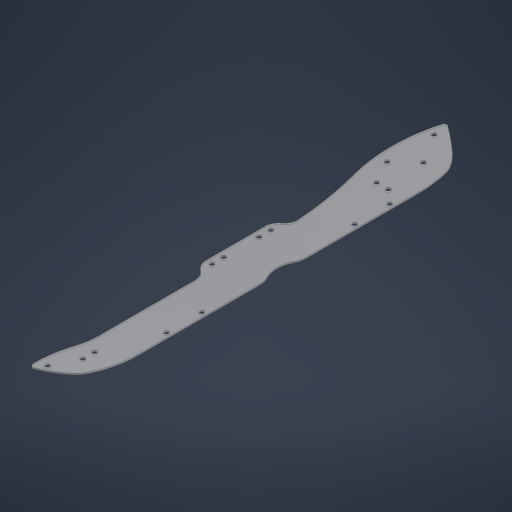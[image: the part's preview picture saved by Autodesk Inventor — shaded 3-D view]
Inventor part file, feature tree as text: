
AUTODESK INVENTOR PART (.ipt)
format: ipt  version: 2024 (Build 280153000, 153)  size: 365,568 bytes
history: native  units: in
note: dims shown in document units (in); Inventor stores cm internally (conversion verified against a paired STEP export)
features: sketch x1, extrude x1, hole x1
ambient origin geometry x8: Origin, YZ Plane, XZ Plane, XY Plane, X Axis, Y Axis, Z Axis, Center Point
bodies: Solid1 (feature_tree)
feature tree (3):
  sketch  "Sketch2"  dims[d3=0.5in d5=0.5in d8=0.0625in d9=0.0in d37=0.25in d46=0.1875in d47=0.75in d48=0.375in d49=0.25in d50=0.5635in d51=1.0in d52=0.8108in d54=0.25in d55=1.0in d58=0.75in d77=0.375in d82=12.75in d83=1.0in d84=0.5in d85=1.5in d86=7.5in d87=2.375in d88=1.445in d89=1.0in d93=0.25in d94=0.25in d95=1.25in d96=2.875in d97=1.0in d99=1.0in d102=1.0in d103=0.5in d104=0.5in d105=3.25in d106=0.3125in d107=3.25in d108=1.5in d109=1.5in d110=3.0in d111=0.25in d112=0.75in d113=0.5in d114=0.75in d115=0.5in d116=0.25in d117=1.25in d118=0.5in d119=0.5in]
  extrude  "Extrusion1"  Depth=0.5in
  hole  "Hole3"  [1 undecoded]
note: 1 required parameter value undecoded (feature->parameter linkage not recoverable at this tier; creation-order binding heuristic only, values carry confidence <= 0.55)
